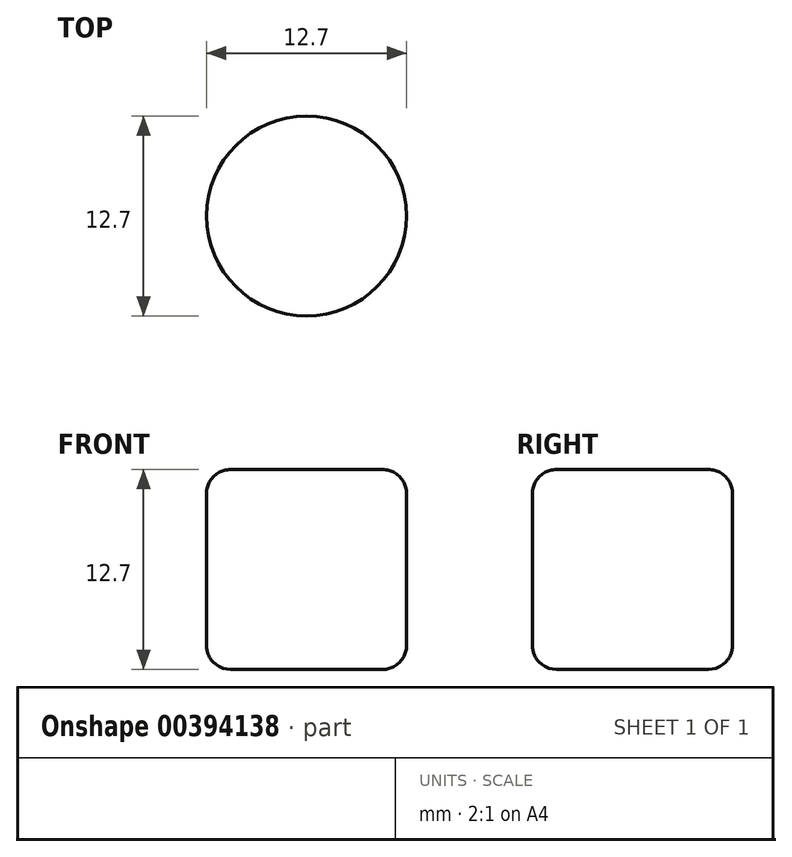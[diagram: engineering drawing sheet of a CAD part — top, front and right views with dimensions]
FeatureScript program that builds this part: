
annotation { "Feature Type Name" : "Feature", "Feature Type Description" : "" }
export const myFeature = defineFeature(function(context is Context, id is Id, definition is map)
    precondition{}
    {
        {
            var Q0;
            Q0=qCreatedBy(makeId("Top.planeOp"),FACE);
            var sketch = newSketch(context, id + "F0", { "sketchPlane" : qUnion([Q0])});
            skCircle(sketch, "E0", {"center": v(0, 0) * mm, "radius": 6.35 * mm});
            skSolve(sketch);
        }
        {
            var Q0;
            Q0=makeQuery(id+"F0.imprint","IMPRINT",FACE,{"disambiguationData":[TD([[makeQuery(id+"F0.imprint","IMPRINT",EDGE,{"derivedFrom":sQuery(id+"F0.wireOp",EDGE,"E0")}),1.0]])]});
            extrude(context, id + "F1", {"entities" : qUnion([Q0]), "endBound" : BoundingType.SYMMETRIC, "depth" : 12.7 * mm});
        }
        {
            var Q0;
            Q0=makeQuery(id+"F1.opExtrude","CAP_EDGE",EDGE,{"disambiguationData":[OSD([sQuery(id+"F0.wireOp",EDGE,"E0")])],"isStart":true});
            fillet(context, id + "F2", {"entities" : qUnion([Q0]), "radius" : 1.52 * mm, "tangentPropagation" : true, "allowEdgeOverflow" : false});
        }
        {
            var Q0;
            Q0=makeQuery(id+"F1.opExtrude","CAP_EDGE",EDGE,{"disambiguationData":[OSD([sQuery(id+"F0.wireOp",EDGE,"E0")])],"isStart":false});
            fillet(context, id + "F3", {"entities" : qUnion([Q0]), "radius" : 1.52 * mm, "tangentPropagation" : true, "allowEdgeOverflow" : false});
        }
    });
